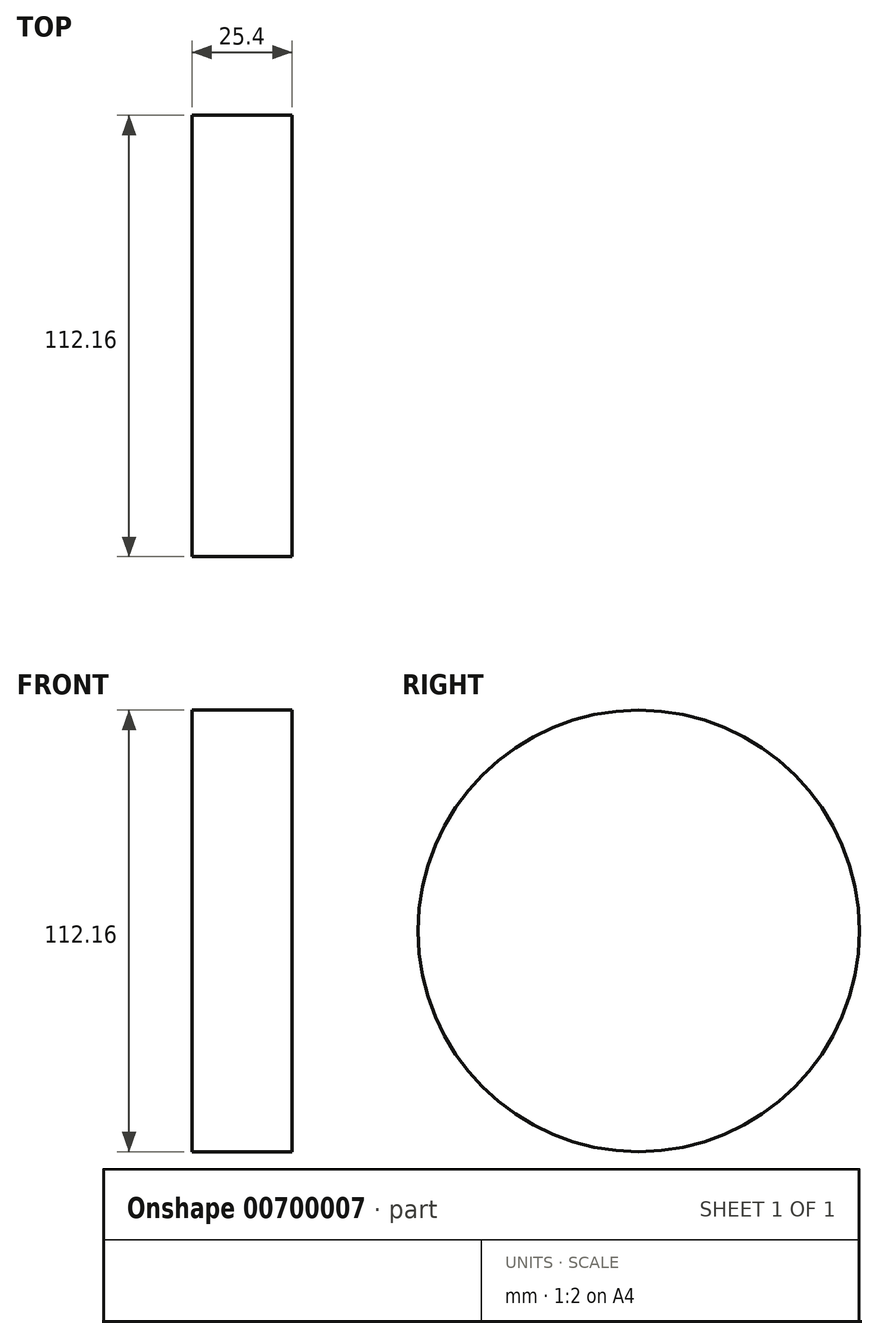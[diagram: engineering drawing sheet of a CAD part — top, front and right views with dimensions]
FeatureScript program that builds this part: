
annotation { "Feature Type Name" : "Feature", "Feature Type Description" : "" }
export const myFeature = defineFeature(function(context is Context, id is Id, definition is map)
    precondition{}
    {
        {
            var Q0;
            Q0=qCreatedBy(makeId("Right.planeOp"),FACE);
            var sketch = newSketch(context, id + "F0", { "sketchPlane" : qUnion([Q0])});
            skCircle(sketch, "E0", {"center": v(0, 0) * mm, "radius": 56.08 * mm});
            skSolve(sketch);
        }
        {
            var Q0;
            Q0=sQuery(id+"F0.wireOp",EDGE,"E0");
            extrude(context, id + "F1", {"bodyType" : ToolBodyType.SURFACE, "surfaceEntities" : qUnion([Q0]), "depth" : 25.4 * mm, "offsetDistance" : 25.4 * mm});
        }
    });
